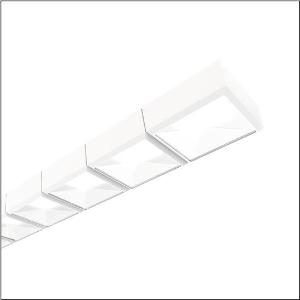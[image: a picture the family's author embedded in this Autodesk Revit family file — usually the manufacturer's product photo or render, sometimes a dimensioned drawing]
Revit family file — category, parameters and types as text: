
# Revit family: scriptus_11_5mz323d04wa
name_source: partatom
category: Lighting Fixtures
units: mm (PartAtom-declared; Revit-internal decimal feet)

## family parameters
Cut with Voids When Loaded = No
Host = Face
Light Source = No
Part Type = Normal
Room Calculation Point = No
Round Connector Dimension = Use Diameter
Shared = No

## types (1)
- Scriptus 11 (1 x LED 4000K / CRI = 80 (unbekannt), 4840 lm / 7230 lm, 4000K)
    Apparent Load = 91 VA
    CIE Flux Codes = - - - 0 100 / 82 95 99 100 100
    Color Rendering = 80
    Color Temperature = 4000K
    Default Elevation = 1800 mm
    Description = Scriptus 11, office luminaire, primary optical cover: lenses, CAT 2 (L<= 3000cd/m²), light emission: direct/indirect distribution, primary light characteristic: symmetric, installation type: suspended mounting, LED, rated luminous flux: 12.070lm, luminous efficacy: 133lm/W, light colour: 840, colour temperature: 4000K, control gear: DALI, with terminal, 5-pole, mains connection: 230V, AC, 50Hz, rated input power: 91W, LED, control gear: ECG DALI, housing, luminaire housing, of aluminium, traffic white (RAL 9016), length: 2.426mm, width: 114mm, height: 57mm, protection rating (complete): IP20, insulation class (complete): insulation class I (protective earthing), certification: CE, ENEC, VDE, protection symbol: F, permissible operating ambient temperature: 0..+35°C, standard: EN 50419, packaging unit: 1 piece
    Height = 57 mm
    Lamp = 1 x LED 4000K / CRI >= 80 (unbekannt)
    Lamp Light Flux = 4840 lm / 7230 lm
    Lamp count = 1
    Length = 2426 mm
    Luminous efficacy = 133 lm/W
    Manufacturer = Siteco
    ModVariant = No
    Model = 5MZ323D04WA
    Mounting Place = Ceiling
    Mounting Type = Pendant
    Number of Poles = 1
    OnlyDefault = Yes
    Power Factor = 1
    Product Name = Scriptus 11
    Product group = office luminaire | ceiling pendant
    ProductGroupID = 903
    Protection Class = Protection class I
    Protection Degree = IP 20
    RLX_Detail_Level = 1
    RLX_Emergency_Light_Flux = 0 lm
    RLX_Emergency_Type = 0
    RLX_Emergency_Type_DB = No
    RlxData = <blob elided: 30225 chars, md5=9074fd09>
    Socket = socket
    Standby Power = 0 W
    System Light Flux = 12070 lm
    System Power = 91 W
    Type Comments = Product without accessories
    Type Image = l_1004839.jpg
    URL = http://relux.com
    VarID = ---
    Voltage = 0 V
    Weight = 0.00 kg
    Width = 114 mm

## geometry (parser evidence)
native form markers: Blend x4, Sweep x13
no freeform markers — native parametric forms only
